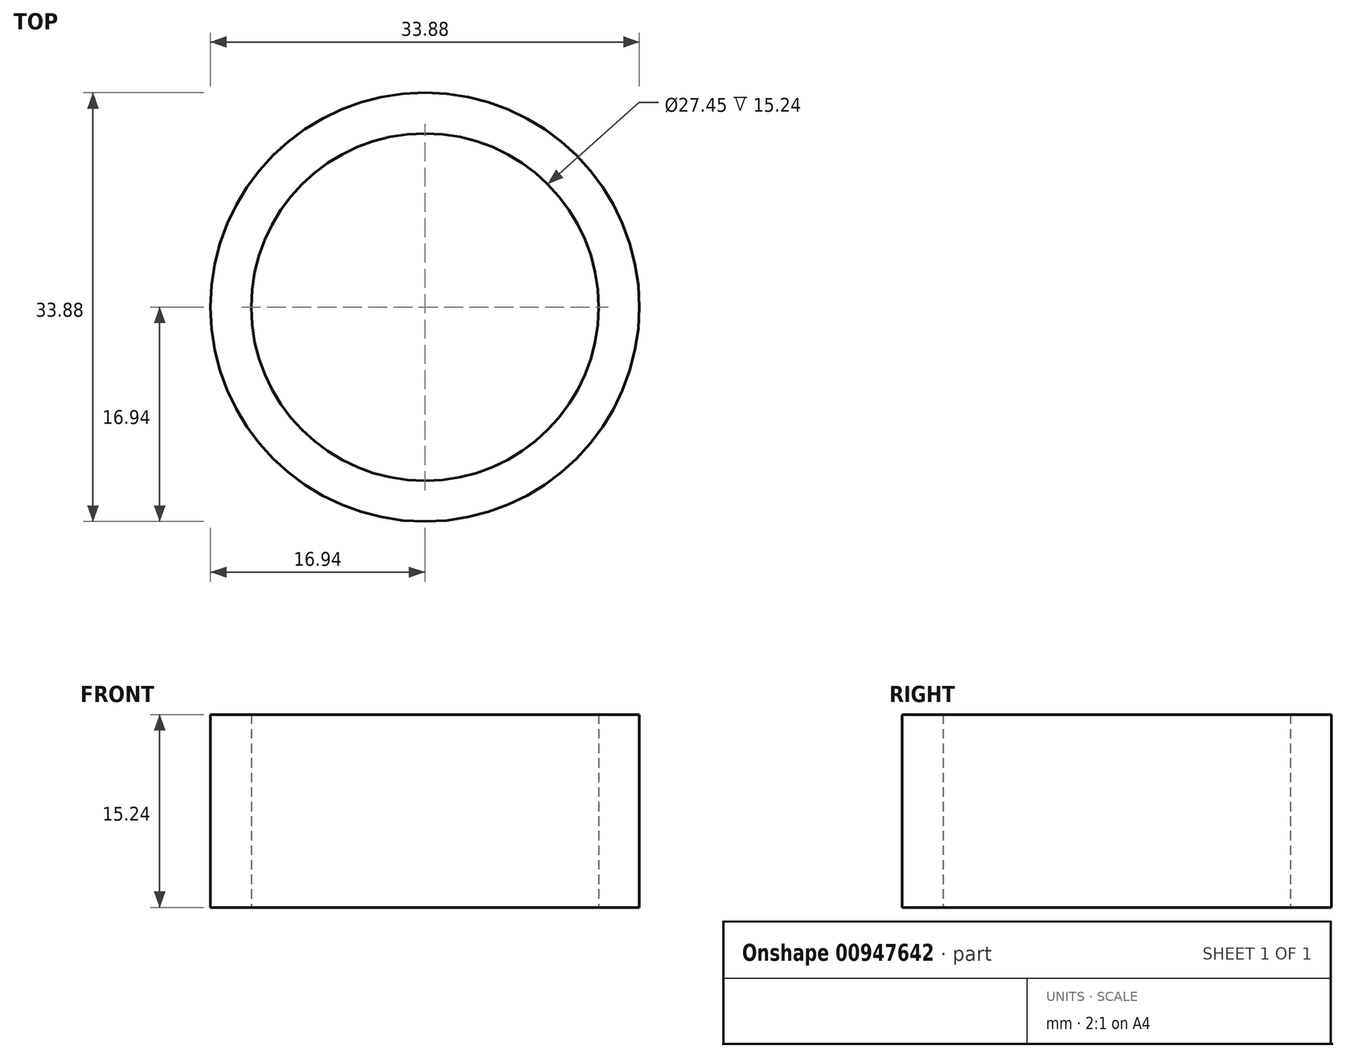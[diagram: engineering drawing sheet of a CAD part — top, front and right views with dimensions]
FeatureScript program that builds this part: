
annotation { "Feature Type Name" : "Feature", "Feature Type Description" : "" }
export const myFeature = defineFeature(function(context is Context, id is Id, definition is map)
    precondition{}
    {
        {
            var Q0;
            Q0=qCreatedBy(makeId("Top.planeOp"),FACE);
            var sketch = newSketch(context, id + "F0", { "sketchPlane" : qUnion([Q0])});
            skCircle(sketch, "E0", {"center": v(0, 0) * mm, "radius": 16.94 * mm});
            skCircle(sketch, "E1", {"center": v(0, 0) * mm, "radius": 13.72 * mm});
            skSolve(sketch);
        }
        {
            var Q0;
            Q0=makeQuery(id+"F0.imprint","IMPRINT",FACE,{"disambiguationData":[TD([[makeQuery(id+"F0.imprint","IMPRINT",EDGE,{"derivedFrom":sQuery(id+"F0.wireOp",EDGE,"E0")}),1.0]])]});
            extrude(context, id + "F1", {"entities" : qUnion([Q0]), "depth" : 15.24 * mm, "offsetDistance" : 25.4 * mm});
        }
    });
